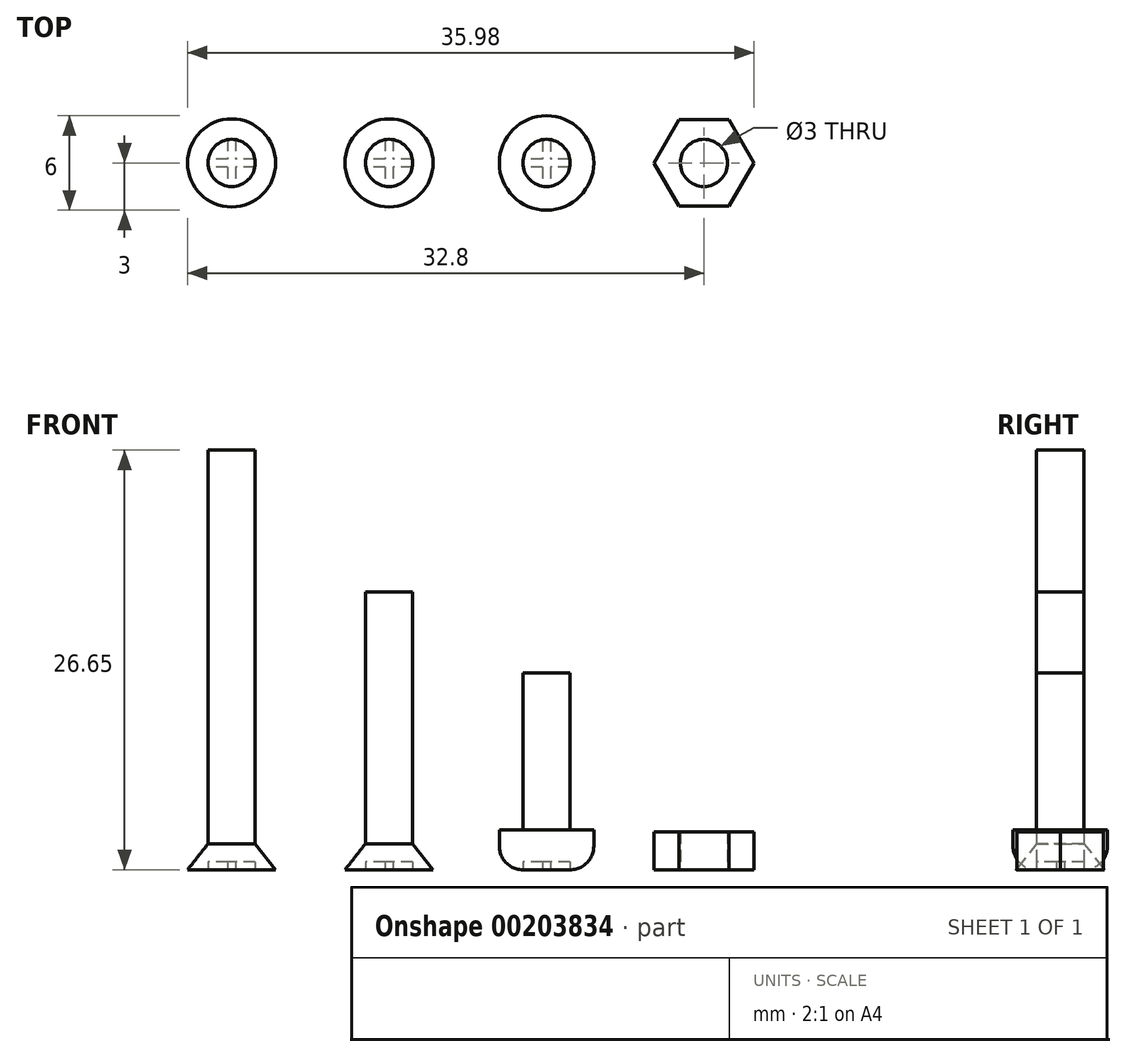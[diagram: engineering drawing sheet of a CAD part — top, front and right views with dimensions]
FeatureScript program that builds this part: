
annotation { "Feature Type Name" : "Feature", "Feature Type Description" : "" }
export const myFeature = defineFeature(function(context is Context, id is Id, definition is map)
    precondition{}
    {
        {
            var Q0;
            Q0=qCreatedBy(makeId("Front.planeOp"),FACE);
            var sketch = newSketch(context, id + "F0", { "sketchPlane" : qUnion([Q0])});
            skLineSegment(sketch, "E0", {"start": v(10, 26.65) * mm, "end": v(11.5, 26.65) * mm});
            skLineSegment(sketch, "E1", {"start": v(11.5, 26.65) * mm, "end": v(11.5, 1.65) * mm});
            skLineSegment(sketch, "E2", {"start": v(11.5, 1.65) * mm, "end": v(12.8, 0) * mm});
            skLineSegment(sketch, "E3", {"start": v(12.8, 0) * mm, "end": v(10, 0) * mm});
            skLineSegment(sketch, "E4", {"start": v(10, 0) * mm, "end": v(10, 26.65) * mm});
            skLineSegment(sketch, "E5", {"start": v(20, 17.65) * mm, "end": v(21.5, 17.65) * mm});
            skLineSegment(sketch, "E6", {"start": v(21.5, 17.65) * mm, "end": v(21.5, 1.65) * mm});
            skLineSegment(sketch, "E7", {"start": v(21.5, 1.65) * mm, "end": v(22.8, 0) * mm});
            skLineSegment(sketch, "E8", {"start": v(22.8, 0) * mm, "end": v(20, 0) * mm});
            skLineSegment(sketch, "E9", {"start": v(20, 0) * mm, "end": v(20, 17.65) * mm});
            skLineSegment(sketch, "E10", {"start": v(30, 12.52) * mm, "end": v(30, 0) * mm});
            skLineSegment(sketch, "E11", {"start": v(30, 0) * mm, "end": v(31.5, 0) * mm});
            skLineSegment(sketch, "E12", {"start": v(33, 1.5) * mm, "end": v(33, 2.52) * mm});
            skLineSegment(sketch, "E13", {"start": v(33, 2.52) * mm, "end": v(31.5, 2.52) * mm});
            skLineSegment(sketch, "E14", {"start": v(31.5, 2.52) * mm, "end": v(31.5, 12.52) * mm});
            skLineSegment(sketch, "E15", {"start": v(31.5, 12.52) * mm, "end": v(30, 12.52) * mm});
            skPoint(sketch, "E16.visualSharp", {"position": v(33, 0) * mm});
            skArc(sketch, "E16.filletArc", {"start": v(31.5, 0) * mm, "mid": v(32.56, 0.44) * mm, "end": v(33, 1.5) * mm});
            skSolve(sketch);
        }
        {
            var Q0;
            Q0=makeQuery(id+"F0.imprint","IMPRINT",FACE,{"disambiguationData":[TD([[makeQuery(id+"F0.imprint","IMPRINT",EDGE,{"derivedFrom":sQuery(id+"F0.wireOp",EDGE,"E0")}),-1.0]])]});
            var Q1;
            Q1=sQuery(id+"F0.wireOp",EDGE,"E4");
            revolve(context, id + "F1", {"entities" : qUnion([Q0]), "axis" : qUnion([Q1]), "revolveType" : RevolveType.FULL});
        }
        {
            var Q0;
            Q0=makeQuery(id+"F0.imprint","IMPRINT",FACE,{"disambiguationData":[TD([[makeQuery(id+"F0.imprint","IMPRINT",EDGE,{"derivedFrom":sQuery(id+"F0.wireOp",EDGE,"E5")}),-1.0]])]});
            var Q1;
            Q1=sQuery(id+"F0.wireOp",EDGE,"E9");
            revolve(context, id + "F2", {"entities" : qUnion([Q0]), "axis" : qUnion([Q1]), "revolveType" : RevolveType.FULL});
        }
        {
            var Q0;
            Q0=makeQuery(id+"F0.imprint","IMPRINT",FACE,{"disambiguationData":[TD([[makeQuery(id+"F0.imprint","IMPRINT",EDGE,{"derivedFrom":sQuery(id+"F0.wireOp",EDGE,"E10")}),1.0]])]});
            var Q1;
            Q1=sQuery(id+"F0.wireOp",EDGE,"E10");
            revolve(context, id + "F3", {"entities" : qUnion([Q0]), "axis" : qUnion([Q1]), "revolveType" : RevolveType.FULL});
        }
        {
            var Q0;
            Q0=qCreatedBy(makeId("Top.planeOp"),FACE);
            var sketch = newSketch(context, id + "F4", { "sketchPlane" : qUnion([Q0])});
            skCircle(sketch, "E17.cCircle", {"center": v(40, 0) * mm, "radius": 2.75 * mm, "construction": true});
            skLineSegment(sketch, "E17.0", {"start": v(43.18, 0) * mm, "end": v(41.59, -2.75) * mm});
            skLineSegment(sketch, "E17.1", {"start": v(41.59, -2.75) * mm, "end": v(38.41, -2.75) * mm});
            skLineSegment(sketch, "E17.2", {"start": v(38.41, -2.75) * mm, "end": v(36.82, 0) * mm});
            skLineSegment(sketch, "E17.3", {"start": v(36.82, 0) * mm, "end": v(38.41, 2.75) * mm});
            skLineSegment(sketch, "E17.4", {"start": v(38.41, 2.75) * mm, "end": v(41.59, 2.75) * mm});
            skLineSegment(sketch, "E17.5", {"start": v(41.59, 2.75) * mm, "end": v(43.18, 0) * mm});
            skPoint(sketch, "E17.0.midPoint", {"position": v(42.38, -1.38) * mm});
            skCircle(sketch, "E18", {"center": v(40, 0) * mm, "radius": 1.5 * mm});
            skSolve(sketch);
        }
        {
            var Q0;
            Q0=makeQuery(id+"F4.imprint","IMPRINT",FACE,{"disambiguationData":[TD([[makeQuery(id+"F4.imprint","IMPRINT",EDGE,{"derivedFrom":sQuery(id+"F4.wireOp",EDGE,"E17.0")}),-1.0]])]});
            extrude(context, id + "F5", {"entities" : qUnion([Q0]), "depth" : 2.4 * mm});
        }
        {
            var Q0;
            Q0=makeQuery(id+"F1.opRevolve","SWEPT_FACE",FACE,{"disambiguationData":[OSD([sQuery(id+"F0.wireOp",EDGE,"E3")])]});
            var sketch = newSketch(context, id + "F6", { "sketchPlane" : qUnion([Q0])});
            skLineSegment(sketch, "E19.bottom", {"start": v(10.25, -1.5) * mm, "end": v(9.75, -1.5) * mm});
            skLineSegment(sketch, "E19.top", {"start": v(10.25, 1.5) * mm, "end": v(9.75, 1.5) * mm});
            skLineSegment(sketch, "E19.left", {"start": v(10.25, -1.5) * mm, "end": v(10.25, -0.25) * mm});
            skLineSegment(sketch, "E19.right", {"start": v(9.75, -1.5) * mm, "end": v(9.75, -0.25) * mm});
            skPoint(sketch, "E19.middle", {"position": v(10, 0) * mm});
            skLineSegment(sketch, "E20.bottom", {"start": v(11.5, -0.25) * mm, "end": v(10.25, -0.25) * mm});
            skLineSegment(sketch, "E20.top", {"start": v(11.5, 0.25) * mm, "end": v(10.25, 0.25) * mm});
            skLineSegment(sketch, "E20.left", {"start": v(11.5, -0.25) * mm, "end": v(11.5, 0.25) * mm});
            skLineSegment(sketch, "E20.right", {"start": v(8.5, -0.25) * mm, "end": v(8.5, 0.25) * mm});
            skLineSegment(sketch, "E21.trimOffspring", {"start": v(9.75, 0.25) * mm, "end": v(8.5, 0.25) * mm});
            skLineSegment(sketch, "E22.trimOffspring", {"start": v(9.75, -0.25) * mm, "end": v(8.5, -0.25) * mm});
            skLineSegment(sketch, "E23.trimOffspring", {"start": v(10.25, 0.25) * mm, "end": v(10.25, 1.5) * mm});
            skLineSegment(sketch, "E24.trimOffspring", {"start": v(9.75, 0.25) * mm, "end": v(9.75, 1.5) * mm});
            skLineSegment(sketch, "E25.bottom", {"start": v(20.25, -1.5) * mm, "end": v(19.75, -1.5) * mm});
            skLineSegment(sketch, "E25.top", {"start": v(20.25, 1.5) * mm, "end": v(19.75, 1.5) * mm});
            skLineSegment(sketch, "E25.left", {"start": v(20.25, -1.5) * mm, "end": v(20.25, -0.25) * mm});
            skLineSegment(sketch, "E25.right", {"start": v(19.75, -1.5) * mm, "end": v(19.75, -0.25) * mm});
            skPoint(sketch, "E25.middle", {"position": v(20, 0) * mm});
            skLineSegment(sketch, "E26.bottom", {"start": v(21.5, -0.25) * mm, "end": v(20.25, -0.25) * mm});
            skLineSegment(sketch, "E26.top", {"start": v(21.5, 0.25) * mm, "end": v(20.25, 0.25) * mm});
            skLineSegment(sketch, "E26.left", {"start": v(21.5, -0.25) * mm, "end": v(21.5, 0.25) * mm});
            skLineSegment(sketch, "E26.right", {"start": v(18.5, -0.25) * mm, "end": v(18.5, 0.25) * mm});
            skLineSegment(sketch, "E27.trimOffspring", {"start": v(19.75, 0.25) * mm, "end": v(18.5, 0.25) * mm});
            skLineSegment(sketch, "E28.trimOffspring", {"start": v(19.75, -0.25) * mm, "end": v(18.5, -0.25) * mm});
            skLineSegment(sketch, "E29.trimOffspring", {"start": v(20.25, 0.25) * mm, "end": v(20.25, 1.5) * mm});
            skLineSegment(sketch, "E30.trimOffspring", {"start": v(19.75, 0.25) * mm, "end": v(19.75, 1.5) * mm});
            skLineSegment(sketch, "E31.bottom", {"start": v(30.25, -1.5) * mm, "end": v(29.75, -1.5) * mm});
            skLineSegment(sketch, "E31.top", {"start": v(30.25, 1.5) * mm, "end": v(29.75, 1.5) * mm});
            skLineSegment(sketch, "E31.left", {"start": v(30.25, -1.5) * mm, "end": v(30.25, -0.25) * mm});
            skLineSegment(sketch, "E31.right", {"start": v(29.75, -1.5) * mm, "end": v(29.75, -0.25) * mm});
            skPoint(sketch, "E31.middle", {"position": v(30, 0) * mm});
            skLineSegment(sketch, "E32.bottom", {"start": v(31.5, -0.25) * mm, "end": v(30.25, -0.25) * mm});
            skLineSegment(sketch, "E32.top", {"start": v(31.5, 0.25) * mm, "end": v(30.25, 0.25) * mm});
            skLineSegment(sketch, "E32.left", {"start": v(31.5, -0.25) * mm, "end": v(31.5, 0.25) * mm});
            skLineSegment(sketch, "E32.right", {"start": v(28.5, -0.25) * mm, "end": v(28.5, 0.25) * mm});
            skLineSegment(sketch, "E33.trimOffspring", {"start": v(29.75, 0.25) * mm, "end": v(28.5, 0.25) * mm});
            skLineSegment(sketch, "E34.trimOffspring", {"start": v(29.75, -0.25) * mm, "end": v(28.5, -0.25) * mm});
            skLineSegment(sketch, "E35.trimOffspring", {"start": v(30.25, 0.25) * mm, "end": v(30.25, 1.5) * mm});
            skLineSegment(sketch, "E36.trimOffspring", {"start": v(29.75, 0.25) * mm, "end": v(29.75, 1.5) * mm});
            skSolve(sketch);
        }
        {
            var Q0;
            Q0=makeQuery(id+"F6.imprint","IMPRINT",FACE,{"disambiguationData":[TD([[makeQuery(id+"F6.imprint","IMPRINT",EDGE,{"derivedFrom":sQuery(id+"F6.wireOp",EDGE,"E19.bottom")}),-1.0]])]});
            var Q1;
            Q1=makeQuery(id+"F6.imprint","IMPRINT",FACE,{"disambiguationData":[TD([[makeQuery(id+"F6.imprint","IMPRINT",EDGE,{"derivedFrom":sQuery(id+"F6.wireOp",EDGE,"E25.bottom")}),-1.0]])]});
            var Q2;
            Q2=makeQuery(id+"F6.imprint","IMPRINT",FACE,{"disambiguationData":[TD([[makeQuery(id+"F6.imprint","IMPRINT",EDGE,{"derivedFrom":sQuery(id+"F6.wireOp",EDGE,"E31.bottom")}),-1.0]])]});
            extrude(context, id + "F7", {"entities" : qUnion([Q0, Q1, Q2]), "operationType" : NewBodyOperationType.REMOVE, "oppositeDirection" : true, "depth" : 0.5 * mm});
        }
    });
